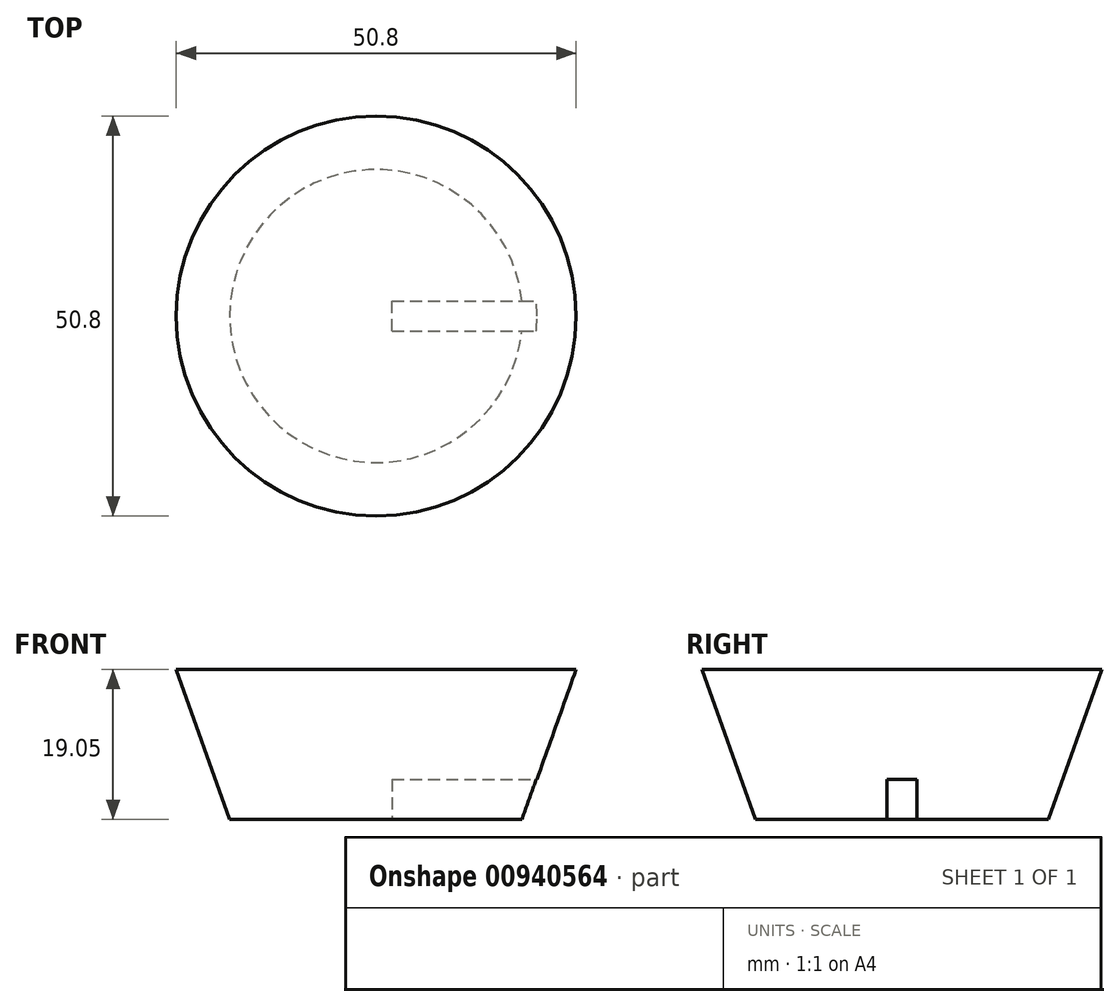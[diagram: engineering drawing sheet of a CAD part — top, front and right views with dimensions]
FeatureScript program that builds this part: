
annotation { "Feature Type Name" : "Feature", "Feature Type Description" : "" }
export const myFeature = defineFeature(function(context is Context, id is Id, definition is map)
    precondition{}
    {
        {
            var Q0;
            Q0=qCreatedBy(makeId("Top.planeOp"),FACE);
            var sketch = newSketch(context, id + "F0", { "sketchPlane" : qUnion([Q0])});
            skLineSegment(sketch, "E0", {"start": v(0, 0) * mm, "end": v(25.4, 0) * mm});
            skCircle(sketch, "E1", {"center": v(0, 0) * mm, "radius": 25.4 * mm});
            skSolve(sketch);
        }
        {
            var Q0;
            Q0=qCreatedBy(makeId("Front.planeOp"),FACE);
            var sketch = newSketch(context, id + "F1", { "sketchPlane" : qUnion([Q0])});
            skLineSegment(sketch, "E2", {"start": v(0, 0) * mm, "end": v(0, -19.05) * mm});
            skSolve(sketch);
        }
        {
            var Q0;
            Q0=sQuery(id+"F1.wireOp",VERTEX,"E2.end");
            var Q1;
            Q1=qCreatedBy(makeId("Top.planeOp"),FACE);
            cPlane(context, id + "F2", {"entities" : qUnion([Q0, Q1]), "cplaneType" : CPlaneType.PLANE_POINT, "offset" : 25.4 * mm, "width" : 152.4 * mm, "height" : 152.4 * mm});
        }
        {
            var Q0;
            Q0=qCreatedBy(id+"F2.planeOp",FACE);
            var sketch = newSketch(context, id + "F3", { "sketchPlane" : qUnion([Q0])});
            skCircle(sketch, "E3", {"center": v(0, 0) * mm, "radius": 18.6 * mm});
            skSolve(sketch);
        }
        {
            var Q0;
            Q0=makeQuery(id+"F0.imprint","IMPRINT",FACE,{"disambiguationData":[TD([[makeQuery(id+"F0.imprint","IMPRINT",EDGE,{"derivedFrom":sQuery(id+"F0.wireOp",EDGE,"E1")}),1.0]])]});
            var Q1;
            Q1=makeQuery(id+"F3.imprint","IMPRINT",FACE,{"disambiguationData":[TD([[makeQuery(id+"F3.imprint","IMPRINT",EDGE,{"derivedFrom":sQuery(id+"F3.wireOp",EDGE,"E3")}),1.0]])]});
            loft(context, id + "F4", {"sheetProfilesArray" : [{ "sheetProfileEntities" : qUnion([Q0]) }, { "sheetProfileEntities" : qUnion([Q1]) }]});
        }
        {
            var Q0;
            Q0=makeQuery(id+"F4.opLoft","CAP_FACE",FACE,{"disambiguationData":[OSD([makeQuery(id+"F3.imprint","IMPRINT",FACE,{"disambiguationData":[TD([[makeQuery(id+"F3.imprint","IMPRINT",EDGE,{"derivedFrom":sQuery(id+"F3.wireOp",EDGE,"E3")}),1.0]])]})])],"isStart":true});
            var sketch = newSketch(context, id + "F5", { "sketchPlane" : qUnion([Q0])});
            skLineSegment(sketch, "E4.bottom", {"start": v(2.01, 1.9) * mm, "end": v(26.45, 1.9) * mm});
            skLineSegment(sketch, "E4.top", {"start": v(2.01, -1.9) * mm, "end": v(26.45, -1.9) * mm});
            skLineSegment(sketch, "E4.left", {"start": v(2.01, 1.9) * mm, "end": v(2.01, -1.9) * mm});
            skLineSegment(sketch, "E4.right", {"start": v(26.45, 1.9) * mm, "end": v(26.45, -1.9) * mm});
            skLineSegment(sketch, "E5", {"start": v(0.28, 0) * mm, "end": v(2.01, 0) * mm});
            skSolve(sketch);
        }
        {
            var Q0;
            Q0 = qSketchRegion(id + "F5", true);
            extrude(context, id + "F6", {"entities" : qUnion([Q0]), "operationType" : NewBodyOperationType.REMOVE, "oppositeDirection" : true, "depth" : 6.35 * mm, "offsetDistance" : 25.4 * mm});
        }
        {
            var Q0;
            Q0=makeQuery(id+"F6.boolean.opBoolean","COPY",FACE,{"derivedFrom":makeQuery(id+"F6.opExtrude","SWEPT_FACE",FACE,{"disambiguationData":[OSD([sQuery(id+"F5.wireOp",EDGE,"E4.left")])]})});
            var Q1;
            Q1=makeQuery(id+"F4.opLoft","SWEPT_FACE",FACE,{"disambiguationData":[OSD([sQuery(id+"F0.wireOp",EDGE,"E1"),sQuery(id+"F3.wireOp",EDGE,"E3")])]});
            extrude(context, id + "F7", {"entities" : qUnion([Q0]), "operationType" : NewBodyOperationType.ADD, "endBound" : BoundingType.UP_TO_SURFACE, "depth" : 25.4 * mm, "endBoundEntityFace" : qUnion([Q1]), "offsetDistance" : 25.4 * mm});
        }
        {
            var Q0;
            {var subQ0=sQuery(id+"F5.wireOp",EDGE,"E4.left");var subQ3=makeQuery(id+"F5.imprint","IMPRINT",VERTEX,{"derivedFrom":subQ0});Q0=makeQuery(id+"F5.imprint","IMPRINT",FACE,{"disambiguationData":[TD([[makeQuery(id+"F5.imprint","IMPRINT",EDGE,{"disambiguationData":[TD([[subQ3,1.0]])],"derivedFrom":subQ0}),1.0]])]});}
            extrude(context, id + "F8", {"entities" : qUnion([Q0]), "operationType" : NewBodyOperationType.REMOVE, "oppositeDirection" : true, "depth" : 5.08 * mm, "offsetDistance" : 25.4 * mm});
        }
        {
            var Q0;
            {var subQ0=sQuery(id+"F5.wireOp",EDGE,"E4.right");Q0=makeQuery(id+"F5.imprint","IMPRINT",FACE,{"disambiguationData":[TD([[makeQuery(id+"F5.imprint","IMPRINT",EDGE,{"derivedFrom":subQ0}),-1.0]])]});}
            extrude(context, id + "F9", {"entities" : qUnion([Q0]), "operationType" : NewBodyOperationType.REMOVE, "oppositeDirection" : true, "depth" : 5.08 * mm, "offsetDistance" : 25.4 * mm});
        }
    });
